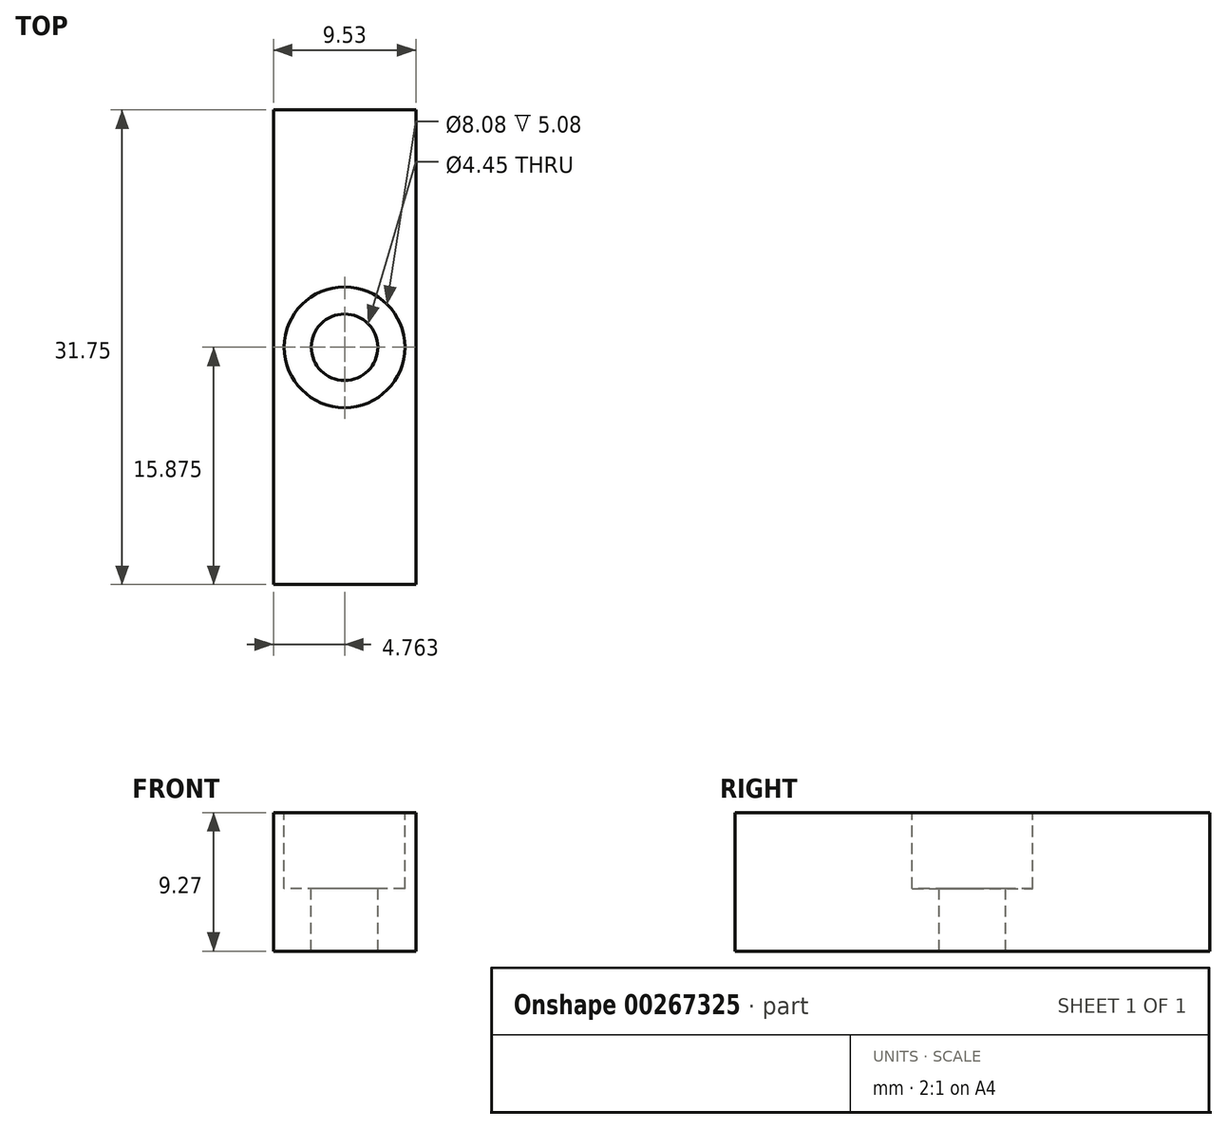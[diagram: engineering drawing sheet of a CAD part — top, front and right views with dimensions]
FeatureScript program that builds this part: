
annotation { "Feature Type Name" : "Feature", "Feature Type Description" : "" }
export const myFeature = defineFeature(function(context is Context, id is Id, definition is map)
    precondition{}
    {
        {
            var Q0;
            Q0=qCreatedBy(makeId("Front.planeOp"),FACE);
            var sketch = newSketch(context, id + "F0", { "sketchPlane" : qUnion([Q0])});
            skLineSegment(sketch, "E0.bottom", {"start": v(0, 9.27) * mm, "end": v(9.52, 9.27) * mm});
            skLineSegment(sketch, "E0.top", {"start": v(0, 0) * mm, "end": v(9.52, 0) * mm});
            skLineSegment(sketch, "E0.left", {"start": v(0, 9.27) * mm, "end": v(0, 0) * mm});
            skLineSegment(sketch, "E0.right", {"start": v(9.52, 9.27) * mm, "end": v(9.52, 0) * mm});
            skSolve(sketch);
        }
        {
            var Q0;
            Q0=makeQuery(id+"F0.imprint","IMPRINT",FACE,{"disambiguationData":[TD([[makeQuery(id+"F0.imprint","IMPRINT",EDGE,{"derivedFrom":sQuery(id+"F0.wireOp",EDGE,"E0.bottom")}),-1.0]])]});
            extrude(context, id + "F1", {"entities" : qUnion([Q0]), "depth" : 31.75 * mm});
        }
        {
            var Q0;
            Q0=makeQuery(id+"F1.opExtrude","SWEPT_FACE",FACE,{"disambiguationData":[OSD([sQuery(id+"F0.wireOp",EDGE,"E0.bottom")])]});
            var sketch = newSketch(context, id + "F2", { "sketchPlane" : qUnion([Q0])});
            skCircle(sketch, "E1", {"center": v(4.76, -15.88) * mm, "radius": 4.04 * mm});
            skSolve(sketch);
        }
        {
            var Q0;
            Q0=makeQuery(id+"F2.imprint","IMPRINT",FACE,{"disambiguationData":[TD([[makeQuery(id+"F2.imprint","IMPRINT",EDGE,{"derivedFrom":sQuery(id+"F2.wireOp",EDGE,"E1")}),1.0]])]});
            extrude(context, id + "F3", {"entities" : qUnion([Q0]), "operationType" : NewBodyOperationType.REMOVE, "oppositeDirection" : true, "depth" : 5.08 * mm});
        }
        {
            var Q0;
            Q0=makeQuery(id+"F3.boolean.opBoolean","COPY",FACE,{"derivedFrom":makeQuery(id+"F3.opExtrude","CAP_FACE",FACE,{"disambiguationData":[OSD([sQuery(id+"F2.wireOp",EDGE,"E1")])],"isStart":false})});
            var sketch = newSketch(context, id + "F4", { "sketchPlane" : qUnion([Q0])});
            skCircle(sketch, "E2", {"center": v(4.76, -15.88) * mm, "radius": 2.22 * mm});
            skSolve(sketch);
        }
        {
            var Q0;
            Q0=makeQuery(id+"F4.imprint","IMPRINT",FACE,{"disambiguationData":[TD([[makeQuery(id+"F4.imprint","IMPRINT",EDGE,{"derivedFrom":sQuery(id+"F4.wireOp",EDGE,"E2")}),1.0]])]});
            extrude(context, id + "F5", {"entities" : qUnion([Q0]), "operationType" : NewBodyOperationType.REMOVE, "endBound" : BoundingType.THROUGH_ALL, "oppositeDirection" : true, "depth" : 25.4 * mm});
        }
    });
